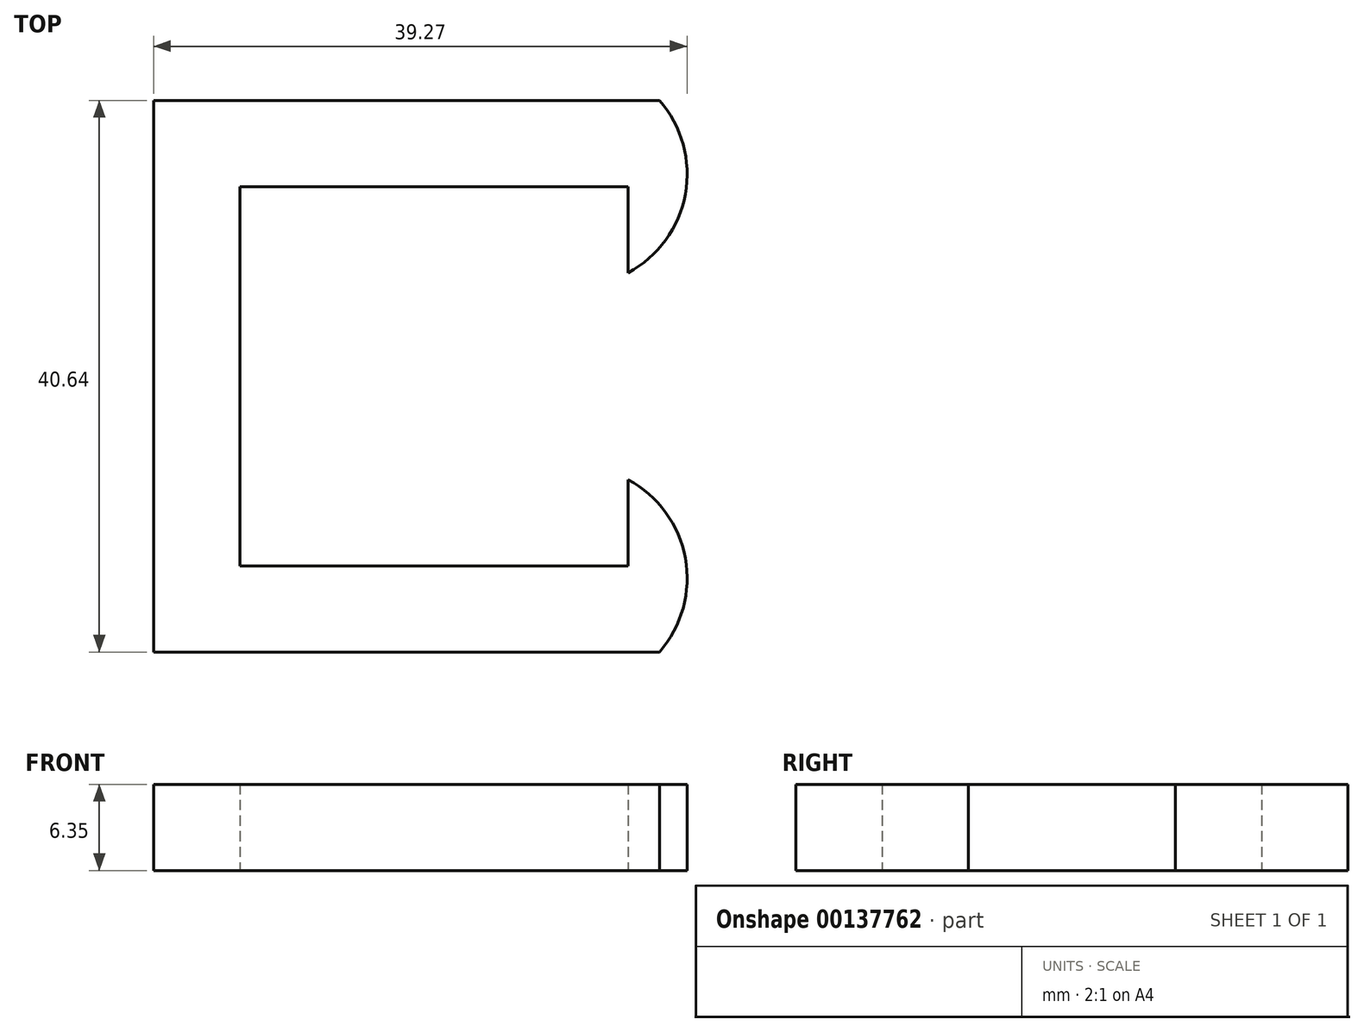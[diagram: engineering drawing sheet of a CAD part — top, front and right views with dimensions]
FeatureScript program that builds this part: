
annotation { "Feature Type Name" : "Feature", "Feature Type Description" : "" }
export const myFeature = defineFeature(function(context is Context, id is Id, definition is map)
    precondition{}
    {
        {
            var Q0;
            Q0=qCreatedBy(makeId("Top.planeOp"),FACE);
            var sketch = newSketch(context, id + "F0", { "sketchPlane" : qUnion([Q0])});
            skLineSegment(sketch, "E0", {"start": v(-18.27, -29.62) * mm, "end": v(-46.84, -29.62) * mm});
            skLineSegment(sketch, "E1", {"start": v(-46.84, -29.62) * mm, "end": v(-46.84, -1.68) * mm});
            skLineSegment(sketch, "E2", {"start": v(-46.84, -1.68) * mm, "end": v(-18.27, -1.68) * mm});
            skLineSegment(sketch, "E3.0", {"start": v(-53.2, 4.67) * mm, "end": v(-15.95, 4.67) * mm});
            skLineSegment(sketch, "E3.1", {"start": v(-53.2, -35.97) * mm, "end": v(-53.2, 4.67) * mm});
            skLineSegment(sketch, "E3.2", {"start": v(-15.95, -35.97) * mm, "end": v(-53.2, -35.97) * mm});
            skLineSegment(sketch, "E4", {"start": v(-18.27, -29.62) * mm, "end": v(-18.27, -23.27) * mm});
            skLineSegment(sketch, "E5", {"start": v(-18.27, -1.68) * mm, "end": v(-18.27, -8.03) * mm});
            skArc(sketch, "E6", {"start": v(-15.95, -35.97) * mm, "mid": v(-14.05, -29.06) * mm, "end": v(-18.27, -23.27) * mm});
            skArc(sketch, "E7", {"start": v(-18.27, -8.03) * mm, "mid": v(-14.05, -2.24) * mm, "end": v(-15.95, 4.67) * mm});
            skSolve(sketch);
        }
        {
            var Q0;
            Q0=makeQuery(id+"F0.imprint","IMPRINT",FACE,{"disambiguationData":[TD([[makeQuery(id+"F0.imprint","IMPRINT",EDGE,{"derivedFrom":sQuery(id+"F0.wireOp",EDGE,"E0")}),1.0]])]});
            extrude(context, id + "F1", {"entities" : qUnion([Q0]), "depth" : 6.35 * mm});
        }
    });
